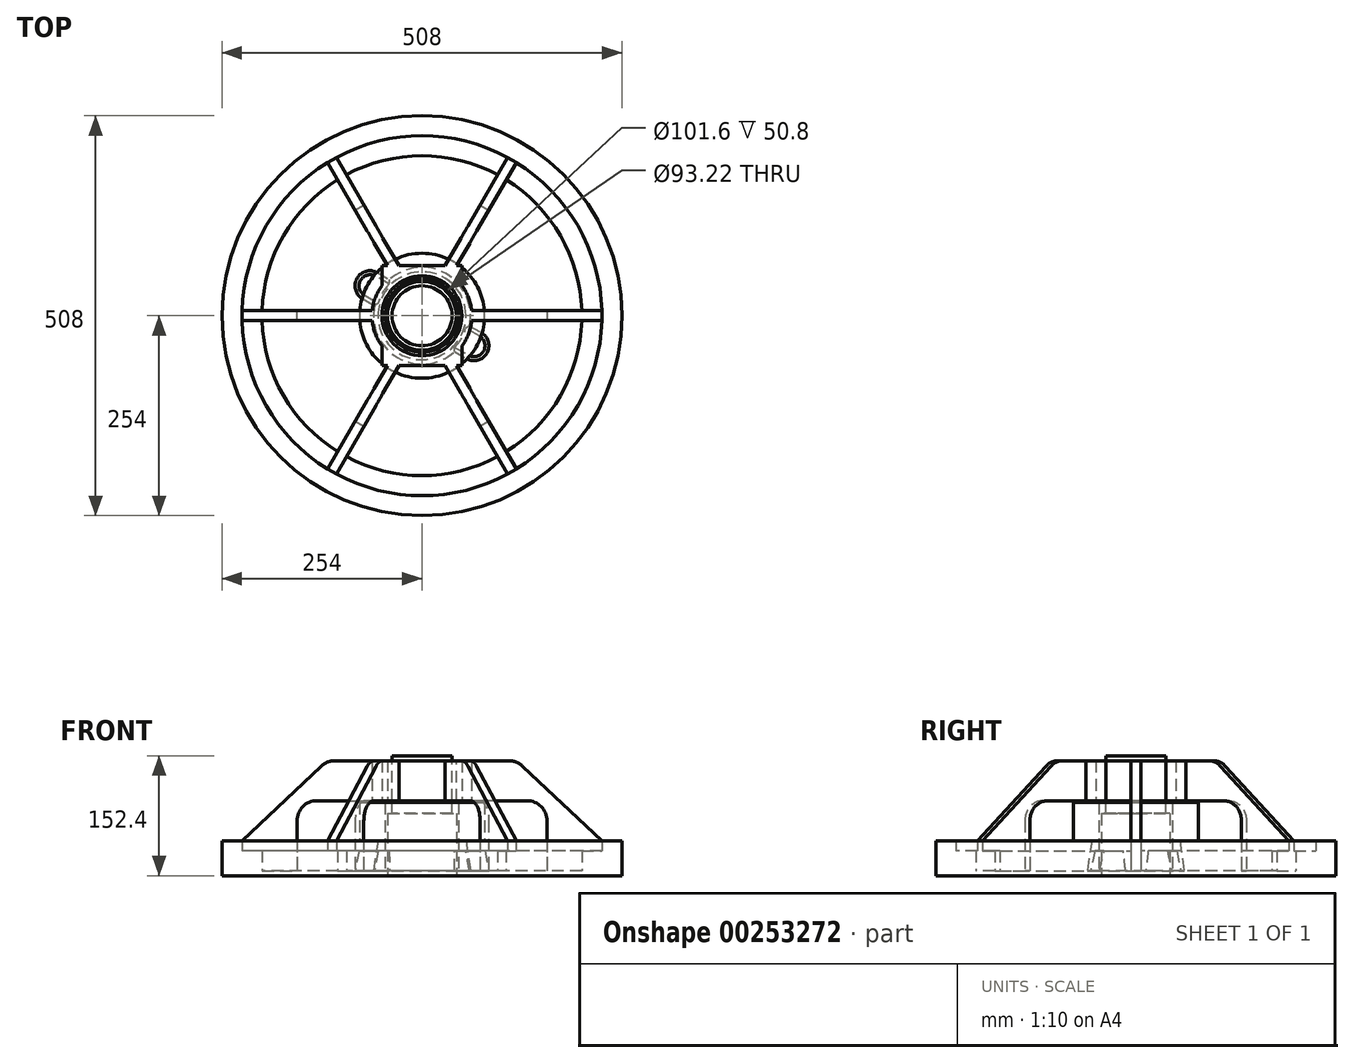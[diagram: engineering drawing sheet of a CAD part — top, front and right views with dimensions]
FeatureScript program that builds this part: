
annotation { "Feature Type Name" : "Feature", "Feature Type Description" : "" }
export const myFeature = defineFeature(function(context is Context, id is Id, definition is map)
    precondition{}
    {
        {
            var Q0;
            Q0=qCreatedBy(makeId("Top.planeOp"),FACE);
            var sketch = newSketch(context, id + "F0", { "sketchPlane" : qUnion([Q0])});
            skCircle(sketch, "E0", {"center": v(0, 0) * mm, "radius": 254 * mm});
            skCircle(sketch, "E1", {"center": v(0, 0) * mm, "radius": 46.6 * mm});
            skSolve(sketch);
        }
        {
            var Q0;
            Q0=makeQuery(id+"F0.imprint","IMPRINT",FACE,{"disambiguationData":[TD([[makeQuery(id+"F0.imprint","IMPRINT",EDGE,{"derivedFrom":sQuery(id+"F0.wireOp",EDGE,"E0")}),1.0]])]});
            extrude(context, id + "F1", {"entities" : qUnion([Q0]), "depth" : 6.35 * mm});
        }
        {
            var Q0;
            Q0=makeQuery(id+"F1.opExtrude","CAP_FACE",FACE,{"disambiguationData":[OSD([sQuery(id+"F0.wireOp",EDGE,"E0")])],"isStart":false});
            var sketch = newSketch(context, id + "F2", { "sketchPlane" : qUnion([Q0])});
            skCircle(sketch, "E2", {"center": v(0, 0) * mm, "radius": 203.2 * mm});
            skSolve(sketch);
        }
        {
            var Q0;
            Q0=makeQuery(id+"F2.imprint","IMPRINT",FACE,{"disambiguationData":[TD([[makeQuery(id+"F2.imprint","IMPRINT",EDGE,{"derivedFrom":sQuery(id+"F2.wireOp",EDGE,"E2")}),-1.0]])]});
            extrude(context, id + "F3", {"entities" : qUnion([Q0]), "operationType" : NewBodyOperationType.ADD, "depth" : 25.4 * mm});
        }
        {
            var Q0;
            Q0=makeQuery(id+"F3.opExtrude","CAP_FACE",FACE,{"disambiguationData":[OSD([sQuery(id+"F0.wireOp",EDGE,"E0"),sQuery(id+"F2.wireOp",EDGE,"E2")])],"isStart":false});
            var sketch = newSketch(context, id + "F4", { "sketchPlane" : qUnion([Q0])});
            skCircle(sketch, "E3", {"center": v(0, 0) * mm, "radius": 228.6 * mm});
            skSolve(sketch);
        }
        {
            var Q0;
            Q0=makeQuery(id+"F4.imprint","IMPRINT",FACE,{"disambiguationData":[TD([[makeQuery(id+"F4.imprint","IMPRINT",EDGE,{"derivedFrom":sQuery(id+"F4.wireOp",EDGE,"E3")}),-1.0]])]});
            extrude(context, id + "F5", {"entities" : qUnion([Q0]), "operationType" : NewBodyOperationType.ADD, "depth" : 12.7 * mm});
        }
        {
            var Q0;
            Q0=makeQuery(id+"F1.opExtrude","CAP_FACE",FACE,{"disambiguationData":[OSD([sQuery(id+"F0.wireOp",EDGE,"E0"),sQuery(id+"F0.wireOp",EDGE,"E1")])],"isStart":false});
            var sketch = newSketch(context, id + "F6", { "sketchPlane" : qUnion([Q0])});
            skCircle(sketch, "E4", {"center": v(0, 0) * mm, "radius": 63.5 * mm});
            skSolve(sketch);
        }
        {
            var Q0;
            Q0=makeQuery(id+"F6.imprint","IMPRINT",FACE,{"disambiguationData":[TD([[makeQuery(id+"F6.imprint","IMPRINT",EDGE,{"derivedFrom":sQuery(id+"F6.wireOp",EDGE,"E4")}),1.0]])]});
            extrude(context, id + "F7", {"entities" : qUnion([Q0]), "operationType" : NewBodyOperationType.ADD, "offsetDistance" : 25.4 * mm, "depth" : 38.1 * mm});
        }
        {
            var Q0;
            Q0=makeQuery(id+"F7.opExtrude","CAP_EDGE",EDGE,{"disambiguationData":[OSD([sQuery(id+"F6.wireOp",EDGE,"E4")])],"isStart":false});
            chamfer(context, id + "F8", {"entities" : qUnion([Q0]), "chamferType" : ChamferType.TWO_OFFSETS, "width1" : 7.62 * mm, "oppositeDirection" : false, "width2" : 50.8 * mm, "tangentPropagation" : true});
        }
        {
            var Q0;
            Q0=makeQuery(id+"F1.opExtrude","CAP_FACE",FACE,{"disambiguationData":[OSD([sQuery(id+"F0.wireOp",EDGE,"E0"),sQuery(id+"F0.wireOp",EDGE,"E1")])],"isStart":false});
            var sketch = newSketch(context, id + "F9", { "sketchPlane" : qUnion([Q0])});
            skLineSegment(sketch, "E5", {"start": v(0, 0) * mm, "end": v(-66, 38.1) * mm, "construction": true});
            skLineSegment(sketch, "E6", {"start": v(0, 0) * mm, "end": v(66, -38.1) * mm, "construction": true});
            skArc(sketch, "E7", {"start": v(-56.47, 54.6) * mm, "mid": v(-82.49, 47.63) * mm, "end": v(-75.52, 21.6) * mm});
            skArc(sketch, "E8", {"start": v(56.47, -54.6) * mm, "mid": v(82.49, -47.63) * mm, "end": v(75.52, -21.6) * mm});
            skLineSegment(sketch, "E9", {"start": v(-56.47, 54.6) * mm, "end": v(-27.31, 37.77) * mm});
            skLineSegment(sketch, "E10", {"start": v(-75.52, 21.6) * mm, "end": v(-46.36, 4.77) * mm});
            skCircle(sketch, "E11.0", {"center": v(0, 0) * mm, "radius": 46.6 * mm});
            skLineSegment(sketch, "E12.trimOffspring", {"start": v(27.31, -37.77) * mm, "end": v(56.47, -54.6) * mm});
            skLineSegment(sketch, "E13.trimOffspring", {"start": v(46.36, -4.77) * mm, "end": v(75.52, -21.6) * mm});
            skSolve(sketch);
        }
        {
            var Q0;
            {var subQ1=sQuery(id+"F9.wireOp",EDGE,"E7");Q0=makeQuery(id+"F9.imprint","IMPRINT",FACE,{"disambiguationData":[TD([[makeQuery(id+"F9.imprint","IMPRINT",EDGE,{"derivedFrom":subQ1}),1.0]])]});}
            var Q1;
            {var subQ1=sQuery(id+"F9.wireOp",EDGE,"E8");Q1=makeQuery(id+"F9.imprint","IMPRINT",FACE,{"disambiguationData":[TD([[makeQuery(id+"F9.imprint","IMPRINT",EDGE,{"derivedFrom":subQ1}),1.0]])]});}
            var Q2;
            {var subQ0=sQuery(id+"F9.wireOp",EDGE,"E11.0");var subQ1=sQuery(id+"F9.wireOp",EDGE,"E9");var subQ2=makeQuery(id+"F9.imprint","INTERSECT",VERTEX,{"derivedFrom":[subQ1,subQ0]});Q2=makeQuery(id+"F9.imprint","IMPRINT",FACE,{"disambiguationData":[TD([[makeQuery(id+"F9.imprint","IMPRINT",EDGE,{"disambiguationData":[TD([[subQ2,-1.0]])],"derivedFrom":subQ0}),-1.0]])]});}
            var Q3;
            {var subQ0=sQuery(id+"F9.wireOp",EDGE,"E12.trimOffspring");var subQ1=sQuery(id+"F9.wireOp",EDGE,"E11.0");var subQ2=makeQuery(id+"F9.imprint","INTERSECT",VERTEX,{"derivedFrom":[subQ1,subQ0]});Q3=makeQuery(id+"F9.imprint","IMPRINT",FACE,{"disambiguationData":[TD([[makeQuery(id+"F9.imprint","IMPRINT",EDGE,{"disambiguationData":[TD([[subQ2,-1.0]])],"derivedFrom":subQ1}),-1.0]])]});}
            extrude(context, id + "F10", {"entities" : qUnion([Q0, Q1, Q2, Q3]), "operationType" : NewBodyOperationType.ADD, "offsetDistance" : 25.4 * mm, "depth" : 25.4 * mm});
        }
        {
            var Q0;
            Q0=makeQuery(id+"F10.opExtrude","CAP_FACE",FACE,{"disambiguationData":[OSD([sQuery(id+"F9.wireOp",EDGE,"E7"),sQuery(id+"F9.wireOp",EDGE,"E9"),sQuery(id+"F9.wireOp",EDGE,"E10"),sQuery(id+"F9.wireOp",EDGE,"E11.0")])],"isStart":false});
            var sketch = newSketch(context, id + "F11", { "sketchPlane" : qUnion([Q0])});
            skLineSegment(sketch, "E14.0.0", {"start": v(-75.52, 21.6) * mm, "end": v(-56.77, 10.78) * mm});
            skArc(sketch, "E14.0.1", {"start": v(-56.77, 10.78) * mm, "mid": v(-50.04, 28.9) * mm, "end": v(-37.72, 43.78) * mm});
            skLineSegment(sketch, "E14.0.2", {"start": v(-37.72, 43.78) * mm, "end": v(-56.47, 54.6) * mm});
            skArc(sketch, "E14.0.3", {"start": v(-56.47, 54.6) * mm, "mid": v(-82.49, 47.62) * mm, "end": v(-75.52, 21.6) * mm});
            skLineSegment(sketch, "E15.0.0", {"start": v(75.52, -21.6) * mm, "end": v(56.77, -10.78) * mm});
            skArc(sketch, "E15.0.1", {"start": v(56.77, -10.78) * mm, "mid": v(50.04, -28.9) * mm, "end": v(37.72, -43.78) * mm});
            skLineSegment(sketch, "E15.0.2", {"start": v(37.72, -43.78) * mm, "end": v(56.47, -54.6) * mm});
            skArc(sketch, "E15.0.3", {"start": v(56.47, -54.6) * mm, "mid": v(82.49, -47.63) * mm, "end": v(75.52, -21.6) * mm});
            skCircle(sketch, "E16", {"center": v(-66, 38.1) * mm, "radius": 4.76 * mm});
            skCircle(sketch, "E17", {"center": v(66, -38.1) * mm, "radius": 4.76 * mm});
            skSolve(sketch);
        }
        {
            var Q0;
            Q0=makeQuery(id+"F10.opExtrude","CAP_EDGE",EDGE,{"disambiguationData":[OSD([sQuery(id+"F9.wireOp",EDGE,"E10")])],"isStart":false});
            var Q1;
            Q1=makeQuery(id+"F10.opExtrude","CAP_EDGE",EDGE,{"disambiguationData":[OSD([sQuery(id+"F9.wireOp",EDGE,"E12.trimOffspring")])],"isStart":false});
            chamfer(context, id + "F12", {"entities" : qUnion([Q0, Q1]), "chamferType" : ChamferType.TWO_OFFSETS, "width1" : 5.08 * mm, "oppositeDirection" : false, "width2" : 25.4 * mm, "tangentPropagation" : true});
        }
        {
            var Q0;
            Q0=makeQuery(id+"F1.opExtrude","CAP_FACE",FACE,{"disambiguationData":[OSD([sQuery(id+"F0.wireOp",EDGE,"E0"),sQuery(id+"F0.wireOp",EDGE,"E1")])],"isStart":false});
            cPlane(context, id + "F13", {"entities" : qUnion([Q0]), "cplaneType" : CPlaneType.OFFSET, "offset" : 88.9 * mm, "width" : 152.4 * mm, "height" : 152.4 * mm});
        }
        {
            var Q0;
            Q0=qCreatedBy(id+"F13.planeOp",FACE);
            var sketch = newSketch(context, id + "F14", { "sketchPlane" : qUnion([Q0])});
            skArc(sketch, "E18", {"start": v(-50.8, 38.1) * mm, "mid": v(-63.5, 0) * mm, "end": v(-50.8, -38.1) * mm});
            skLineSegment(sketch, "E19.bottom", {"start": v(-50.8, 63.5) * mm, "end": v(50.8, 63.5) * mm});
            skLineSegment(sketch, "E19.top", {"start": v(-50.8, -63.5) * mm, "end": v(50.8, -63.5) * mm});
            skLineSegment(sketch, "E19.left", {"start": v(-50.8, 63.5) * mm, "end": v(-50.8, 38.1) * mm});
            skLineSegment(sketch, "E19.right", {"start": v(50.8, 63.5) * mm, "end": v(50.8, 38.1) * mm});
            skArc(sketch, "E20.trimOffspring", {"start": v(50.8, -38.1) * mm, "mid": v(63.5, 0) * mm, "end": v(50.8, 38.1) * mm});
            skLineSegment(sketch, "E21.trimOffspring", {"start": v(-50.8, -38.1) * mm, "end": v(-50.8, -63.5) * mm});
            skLineSegment(sketch, "E22.trimOffspring", {"start": v(50.8, -38.1) * mm, "end": v(50.8, -63.5) * mm});
            skCircle(sketch, "E23", {"center": v(0, 0) * mm, "radius": 50.8 * mm});
            skSolve(sketch);
        }
        {
            var Q0;
            Q0=makeQuery(id+"F14.imprint","IMPRINT",FACE,{"disambiguationData":[TD([[makeQuery(id+"F14.imprint","IMPRINT",EDGE,{"derivedFrom":sQuery(id+"F14.wireOp",EDGE,"E18")}),1.0]])]});
            extrude(context, id + "F15", {"entities" : qUnion([Q0]), "depth" : 50.8 * mm});
        }
        {
            var Q0;
            Q0=qCreatedBy(makeId("Front.planeOp"),FACE);
            var sketch = newSketch(context, id + "F16", { "sketchPlane" : qUnion([Q0])});
            skLineSegment(sketch, "E24", {"start": v(-57.15, 146.05) * mm, "end": v(-120.65, 146.05) * mm});
            skLineSegment(sketch, "E25", {"start": v(-120.65, 146.05) * mm, "end": v(-228.6, 44.45) * mm});
            skLineSegment(sketch, "E26", {"start": v(-158.75, 95.25) * mm, "end": v(-158.75, 6.35) * mm});
            skLineSegment(sketch, "E27", {"start": v(-228.6, 44.45) * mm, "end": v(-228.6, 6.35) * mm});
            skLineSegment(sketch, "E28.0.0", {"start": v(-228.6, 6.35) * mm, "end": v(-158.75, 6.35) * mm});
            skPoint(sketch, "E29.orphan", {"position": v(-203.2, 6.35) * mm});
            skPoint(sketch, "E30.0.end.orphan", {"position": v(228.6, 44.45) * mm});
            skPoint(sketch, "E31.orphan", {"position": v(203.2, 6.35) * mm});
            skLineSegment(sketch, "E32.right", {"start": v(-57.15, 146.05) * mm, "end": v(-57.15, 95.25) * mm});
            skLineSegment(sketch, "E33.0", {"start": v(-59, 31.75) * mm, "end": v(-79.96, 31.75) * mm});
            skLineSegment(sketch, "E34.0", {"start": v(-55.88, 44.45) * mm, "end": v(55.88, 44.45) * mm});
            skLineSegment(sketch, "E35.0.0", {"start": v(-203.2, 6.35) * mm, "end": v(203.2, 6.35) * mm});
            skLineSegment(sketch, "E36.0.1", {"start": v(50.8, 146.05) * mm, "end": v(63.5, 146.05) * mm});
            skLineSegment(sketch, "E36.0.3", {"start": v(50.8, 146.05) * mm, "end": v(-50.8, 146.05) * mm});
            skLineSegment(sketch, "E36.0.5", {"start": v(-50.8, 146.05) * mm, "end": v(-63.5, 146.05) * mm});
            skLineSegment(sketch, "E36.0.7", {"start": v(-50.8, 146.05) * mm, "end": v(50.8, 146.05) * mm});
            skLineSegment(sketch, "E37", {"start": v(-158.75, 95.25) * mm, "end": v(-57.15, 95.25) * mm});
            skSolve(sketch);
        }
        {
            var Q0;
            Q0=makeQuery(id+"F16.imprint","IMPRINT",FACE,{"disambiguationData":[TD([[makeQuery(id+"F16.imprint","IMPRINT",EDGE,{"derivedFrom":sQuery(id+"F16.wireOp",EDGE,"a781dbd9-89e4-435a-aec9-d33398cd39ac")}),1.0]])]});
            var Q1;
            Q1=makeQuery(id+"F16.imprint","IMPRINT",FACE,{"disambiguationData":[TD([[makeQuery(id+"F16.imprint","IMPRINT",EDGE,{"derivedFrom":sQuery(id+"F16.wireOp",EDGE,"E24")}),1.0]])]});
            extrude(context, id + "F17", {"entities" : qUnion([Q0, Q1]), "endBound" : BoundingType.SYMMETRIC, "depth" : 12.7 * mm});
        }
        {
            var Q0;
            Q0=makeQuery(id+"F17.opExtrude","SWEPT_EDGE",EDGE,{"disambiguationData":[OSD([sQuery(id+"F16.wireOp",EDGE,"E24"),sQuery(id+"F16.wireOp",EDGE,"E25")])]});
            var Q1;
            Q1=makeQuery(id+"F17.opExtrude","SWEPT_EDGE",EDGE,{"disambiguationData":[OSD([sQuery(id+"F16.wireOp",EDGE,"E26"),sQuery(id+"F16.wireOp",EDGE,"E37")])]});
            fillet(context, id + "F18", {"entities" : qUnion([Q0, Q1]), "radius" : 25.4 * mm, "tangentPropagation" : true, "allowEdgeOverflow" : false});
        }
        {
            var Q0;
            Q0=makeQuery(id+"F17.opExtrude","SWEPT_BODY",BODY,{"disambiguationData":[OSD([sQuery(id+"F16.wireOp",EDGE,"a781dbd9-89e4-435a-aec9-d33398cd39ac"),sQuery(id+"F16.wireOp",EDGE,"E24"),sQuery(id+"F16.wireOp",EDGE,"E25"),sQuery(id+"F16.wireOp",EDGE,"KqElCDLo-RaIw-nRQ4-dxWm-YjDePZ9qcHa3"),sQuery(id+"F16.wireOp",EDGE,"E26"),sQuery(id+"F16.wireOp",EDGE,"E27"),sQuery(id+"F16.wireOp",EDGE,"E28.0.0")])]});
            var Q1;
            {var subQ0=sQuery(id+"F0.wireOp",EDGE,"E1");Q1=makeQuery(id+"F7.boolean.opBoolean","MERGE",FACE,{"derivedFrom":[makeQuery(id+"F1.opExtrude","SWEPT_FACE",FACE,{"disambiguationData":[OSD([subQ0])]}),makeQuery(id+"F7.opExtrude","SWEPT_FACE",FACE,{"disambiguationData":[OSD([subQ0])]})]});}
            circularPattern(context, id + "F19", {"entities" : qUnion([Q0]), "axis" : qUnion([Q1]), "angle" : 360 * degree, "instanceCount" : 6, "equalSpace" : true});
        }
        {
            var Q0;
            Q0=makeQuery(id+"F15.opExtrude","SWEPT_BODY",BODY,{"disambiguationData":[OSD([sQuery(id+"F14.wireOp",EDGE,"E18"),sQuery(id+"F14.wireOp",EDGE,"E19.bottom"),sQuery(id+"F14.wireOp",EDGE,"E19.top"),sQuery(id+"F14.wireOp",EDGE,"E19.left"),sQuery(id+"F14.wireOp",EDGE,"E19.right"),sQuery(id+"F14.wireOp",EDGE,"E20.trimOffspring"),sQuery(id+"F14.wireOp",EDGE,"E21.trimOffspring"),sQuery(id+"F14.wireOp",EDGE,"E22.trimOffspring"),sQuery(id+"F14.wireOp",EDGE,"E23")])]});
            var Q1;
            Q1=makeQuery(id+"F17.opExtrude","SWEPT_BODY",BODY,{"disambiguationData":[OSD([sQuery(id+"F16.wireOp",EDGE,"a781dbd9-89e4-435a-aec9-d33398cd39ac"),sQuery(id+"F16.wireOp",EDGE,"E24"),sQuery(id+"F16.wireOp",EDGE,"E25"),sQuery(id+"F16.wireOp",EDGE,"KqElCDLo-RaIw-nRQ4-dxWm-YjDePZ9qcHa3"),sQuery(id+"F16.wireOp",EDGE,"E26"),sQuery(id+"F16.wireOp",EDGE,"E27"),sQuery(id+"F16.wireOp",EDGE,"E28.0.0")])]});
            var Q2;
            Q2=makeQuery(id+"F19.opPattern","COPY",BODY,{"derivedFrom":makeQuery(id+"F17.opExtrude","SWEPT_BODY",BODY,{"disambiguationData":[OSD([sQuery(id+"F16.wireOp",EDGE,"a781dbd9-89e4-435a-aec9-d33398cd39ac"),sQuery(id+"F16.wireOp",EDGE,"E24"),sQuery(id+"F16.wireOp",EDGE,"E25"),sQuery(id+"F16.wireOp",EDGE,"KqElCDLo-RaIw-nRQ4-dxWm-YjDePZ9qcHa3"),sQuery(id+"F16.wireOp",EDGE,"E26"),sQuery(id+"F16.wireOp",EDGE,"E27"),sQuery(id+"F16.wireOp",EDGE,"E28.0.0")])]}),"instanceName":"5"});
            var Q3;
            Q3=makeQuery(id+"F19.opPattern","COPY",BODY,{"derivedFrom":makeQuery(id+"F17.opExtrude","SWEPT_BODY",BODY,{"disambiguationData":[OSD([sQuery(id+"F16.wireOp",EDGE,"a781dbd9-89e4-435a-aec9-d33398cd39ac"),sQuery(id+"F16.wireOp",EDGE,"E24"),sQuery(id+"F16.wireOp",EDGE,"E25"),sQuery(id+"F16.wireOp",EDGE,"KqElCDLo-RaIw-nRQ4-dxWm-YjDePZ9qcHa3"),sQuery(id+"F16.wireOp",EDGE,"E26"),sQuery(id+"F16.wireOp",EDGE,"E27"),sQuery(id+"F16.wireOp",EDGE,"E28.0.0")])]}),"instanceName":"4"});
            var Q4;
            Q4=makeQuery(id+"F19.opPattern","COPY",BODY,{"derivedFrom":makeQuery(id+"F17.opExtrude","SWEPT_BODY",BODY,{"disambiguationData":[OSD([sQuery(id+"F16.wireOp",EDGE,"a781dbd9-89e4-435a-aec9-d33398cd39ac"),sQuery(id+"F16.wireOp",EDGE,"E24"),sQuery(id+"F16.wireOp",EDGE,"E25"),sQuery(id+"F16.wireOp",EDGE,"KqElCDLo-RaIw-nRQ4-dxWm-YjDePZ9qcHa3"),sQuery(id+"F16.wireOp",EDGE,"E26"),sQuery(id+"F16.wireOp",EDGE,"E27"),sQuery(id+"F16.wireOp",EDGE,"E28.0.0")])]}),"instanceName":"3"});
            var Q5;
            Q5=makeQuery(id+"F19.opPattern","COPY",BODY,{"derivedFrom":makeQuery(id+"F17.opExtrude","SWEPT_BODY",BODY,{"disambiguationData":[OSD([sQuery(id+"F16.wireOp",EDGE,"a781dbd9-89e4-435a-aec9-d33398cd39ac"),sQuery(id+"F16.wireOp",EDGE,"E24"),sQuery(id+"F16.wireOp",EDGE,"E25"),sQuery(id+"F16.wireOp",EDGE,"KqElCDLo-RaIw-nRQ4-dxWm-YjDePZ9qcHa3"),sQuery(id+"F16.wireOp",EDGE,"E26"),sQuery(id+"F16.wireOp",EDGE,"E27"),sQuery(id+"F16.wireOp",EDGE,"E28.0.0")])]}),"instanceName":"2"});
            var Q6;
            Q6=makeQuery(id+"F19.opPattern","COPY",BODY,{"derivedFrom":makeQuery(id+"F17.opExtrude","SWEPT_BODY",BODY,{"disambiguationData":[OSD([sQuery(id+"F16.wireOp",EDGE,"a781dbd9-89e4-435a-aec9-d33398cd39ac"),sQuery(id+"F16.wireOp",EDGE,"E24"),sQuery(id+"F16.wireOp",EDGE,"E25"),sQuery(id+"F16.wireOp",EDGE,"KqElCDLo-RaIw-nRQ4-dxWm-YjDePZ9qcHa3"),sQuery(id+"F16.wireOp",EDGE,"E26"),sQuery(id+"F16.wireOp",EDGE,"E27"),sQuery(id+"F16.wireOp",EDGE,"E28.0.0")])]}),"instanceName":"1"});
            booleanBodies(context, id + "F20", {"operationType" : BooleanOperationType.UNION, "tools" : qUnion([Q0, Q1, Q2, Q3, Q4, Q5, Q6])});
        }
        {
            var Q0;
            Q0=makeQuery(id+"F15.opExtrude","SWEPT_BODY",BODY,{"disambiguationData":[OSD([sQuery(id+"F14.wireOp",EDGE,"E18"),sQuery(id+"F14.wireOp",EDGE,"E19.bottom"),sQuery(id+"F14.wireOp",EDGE,"E19.top"),sQuery(id+"F14.wireOp",EDGE,"E19.left"),sQuery(id+"F14.wireOp",EDGE,"E19.right"),sQuery(id+"F14.wireOp",EDGE,"E20.trimOffspring"),sQuery(id+"F14.wireOp",EDGE,"E21.trimOffspring"),sQuery(id+"F14.wireOp",EDGE,"E22.trimOffspring"),sQuery(id+"F14.wireOp",EDGE,"E23")])]});
            var Q1;
            Q1=makeQuery(id+"F1.opExtrude","SWEPT_BODY",BODY,{"disambiguationData":[OSD([sQuery(id+"F0.wireOp",EDGE,"E0"),sQuery(id+"F0.wireOp",EDGE,"E1")])]});
            booleanBodies(context, id + "F21", {"operationType" : BooleanOperationType.UNION, "tools" : qUnion([Q0, Q1])});
        }
        {
            var Q0;
            Q0=makeQuery(id+"F1.opExtrude","CAP_FACE",FACE,{"disambiguationData":[OSD([sQuery(id+"F0.wireOp",EDGE,"E0"),sQuery(id+"F0.wireOp",EDGE,"E1")])],"isStart":true});
            var sketch = newSketch(context, id + "F22", { "sketchPlane" : qUnion([Q0])});
            skCircle(sketch, "E38", {"center": v(0, 0) * mm, "radius": 43.66 * mm});
            skSolve(sketch);
        }
        {
            var Q0;
            Q0=makeQuery(id+"F22.imprint","IMPRINT",FACE,{"disambiguationData":[TD([[makeQuery(id+"F22.imprint","IMPRINT",EDGE,{"derivedFrom":sQuery(id+"F22.wireOp",EDGE,"E38")}),1.0]])]});
            extrude(context, id + "F23", {"entities" : qUnion([Q0]), "oppositeDirection" : true, "offsetDistance" : 25.4 * mm, "depth" : 152.4 * mm});
        }
        {
            var Q0;
            Q0=makeQuery(id+"F23.opExtrude","CAP_FACE",FACE,{"disambiguationData":[OSD([sQuery(id+"F22.wireOp",EDGE,"E38")])],"isStart":false});
            var sketch = newSketch(context, id + "F24", { "sketchPlane" : qUnion([Q0])});
            skCircle(sketch, "E39.0.0", {"center": v(0, 0) * mm, "radius": 43.66 * mm});
            skCircle(sketch, "E40", {"center": v(0, 0) * mm, "radius": 38.1 * mm});
            skSolve(sketch);
        }
        {
            var Q0;
            Q0=makeQuery(id+"F24.imprint","IMPRINT",FACE,{"disambiguationData":[TD([[makeQuery(id+"F24.imprint","IMPRINT",EDGE,{"derivedFrom":sQuery(id+"F24.wireOp",EDGE,"E39.0.0")}),-1.0]])]});
            extrude(context, id + "F25", {"entities" : qUnion([Q0]), "operationType" : NewBodyOperationType.REMOVE, "oppositeDirection" : true, "offsetDistance" : 25.4 * mm, "depth" : 73.4 * mm});
        }
        {
            var Q0;
            Q0=makeQuery(id+"F7.opExtrude","CAP_FACE",FACE,{"disambiguationData":[OSD([sQuery(id+"F0.wireOp",EDGE,"E1"),sQuery(id+"F6.wireOp",EDGE,"E4")])],"isStart":false});
            var sketch = newSketch(context, id + "F26", { "sketchPlane" : qUnion([Q0])});
            skCircle(sketch, "E41.0", {"center": v(0, 0) * mm, "radius": 46.6 * mm});
            skCircle(sketch, "E42", {"center": v(0, 0) * mm, "radius": 79.38 * mm});
            skSolve(sketch);
        }
        {
            var Q0;
            Q0=makeQuery(id+"F26.imprint","IMPRINT",FACE,{"disambiguationData":[TD([[makeQuery(id+"F26.imprint","IMPRINT",EDGE,{"derivedFrom":sQuery(id+"F26.wireOp",EDGE,"E42")}),1.0]])]});
            var Q1;
            Q1=makeQuery(id+"F26.imprint","IMPRINT",FACE,{"disambiguationData":[TD([[makeQuery(id+"F26.imprint","IMPRINT",EDGE,{"derivedFrom":sQuery(id+"F26.wireOp",EDGE,"E41.0")}),-1.0]])]});
            extrude(context, id + "F27", {"entities" : qUnion([Q0, Q1]), "operationType" : NewBodyOperationType.ADD, "depth" : 48.77 * mm, "offsetDistance" : 25.4 * mm});
        }
    });
